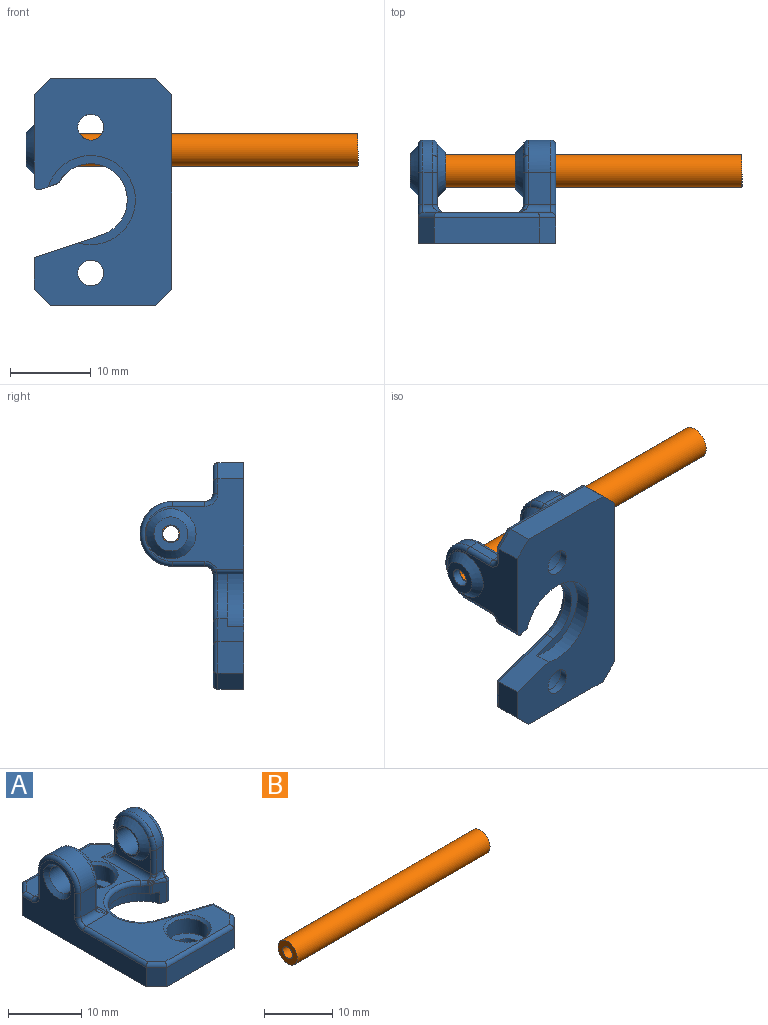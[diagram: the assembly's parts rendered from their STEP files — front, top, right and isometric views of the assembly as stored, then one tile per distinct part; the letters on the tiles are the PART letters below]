
ASSEMBLY  parts=2 mates=1
PART A: 97 faces, bbox 18x28x13.1 mm
  f0: plane 26.8x15.8mm, normal (0,0,1), area 177.3mm2, adj f20,f22,f23,f24,f25,f45,f46,f51
  f1: plane 12.2x11.14mm, normal (1,0,0), area 62.8mm2, adj f3,f34,f49,f56,f58,f60,f62,f64
  f2: plane 24x12.2mm, normal (-1,0,0), area 112.1mm2, adj f3,f26,f36,f48,f63,f65,f67,f69
  f3: plane 28x17mm, normal (0,0,-1), area 336.3mm2, adj f1,f2,f6,f8,f9,f10,f26,f27
  f4: cylinder r=2.85mm len=5.7mm, axis (0,0,-1), area 43mm2, adj f42,f45
  f5: cylinder r=2.85mm len=5.7mm, axis (0,0,-1), area 43mm2, adj f41,f46
  f6: plane 8.43x3.2mm, normal (0.32,0.95,0), area 22.1mm2, adj f3,f7,f8,f30,f31,f53
  f7: cylinder r=4.5mm len=8.77mm, axis (0,0,-1), area 20.9mm2, adj f6,f31,f50,f51,f52,f87
  f8: plane 3.9x3.2mm, normal (1,0,0), area 12.5mm2, adj f3,f6,f27,f55
  f9: plane 3.6x2.01mm, normal (-0.34,-0.94,0), area 5.2mm2, adj f3,f30,f31,f54,f85,f87,f95
  f10: plane 13x3.2mm, normal (0,-1,0), area 41.6mm2, adj f3,f26,f27,f59
  f11: plane 4x1.2mm, normal (0,1,0), area 4.8mm2, adj f20,f28,f62,f76
  f12: plane 6.8x5.78mm, normal (-1,0,0), area 11.6mm2, adj f22,f38,f76,f77,f79,f80
  f13: plane 4.1x1.21mm, normal (0,-1,0), area 4.8mm2, adj f19,f28,f58,f80,f81
  f14: plane 4x2.8mm, normal (0,1,0), area 11.2mm2, adj f23,f29,f71,f93
  f15: plane 4x2.8mm, normal (0,-1,0), area 11.2mm2, adj f25,f29,f67,f89
  f16: plane 6.8x5.78mm, normal (1,0,0), area 11.6mm2, adj f24,f40,f89,f90,f92,f93
  f17: cylinder r=2.05mm len=4.4mm, axis (-1,0,0), area 56.7mm2, adj f36,f39
  f18: cylinder r=2.05mm len=4.1mm, axis (-1,0,0), area 43.8mm2, adj f32,f37
  f19: bspline ~2.84x1.17mm, area 1.4mm2, adj f13,f54,f56,f82,f83
  f20: cylinder r=1mm len=2.8mm, axis (-1,0,0), area 3.1mm2, adj f0,f11,f64,f75
  f21: bspline ~1.22x1.21mm, area 0.1mm2, adj f22,f52,f83,f85
  f22: cylinder r=1mm len=8.5mm, axis (0,-1,0), area 11.5mm2, adj f0,f12,f21,f50,f75,f81,f82
  f23: cylinder r=1mm len=4.4mm, axis (-1,0,0), area 5.7mm2, adj f0,f14,f73,f94
  f24: cylinder r=1mm len=10mm, axis (0,1,0), area 13.2mm2, adj f0,f16,f88,f94
  f25: cylinder r=1mm len=4.4mm, axis (1,0,0), area 5.7mm2, adj f0,f15,f65,f88
  f26: plane 3.2x2mm, normal (-0.71,-0.71,0), area 9.1mm2, adj f2,f3,f10,f61
  f27: plane 3.2x2mm, normal (0.71,-0.71,0), area 9.1mm2, adj f3,f8,f10,f57
  f28: cylinder r=4mm len=8mm, axis (-1,0,0), area 15.1mm2, adj f11,f13,f60,f77,f78,f79
  f29: cylinder r=4mm len=8mm, axis (1,0,0), area 35.2mm2, adj f14,f15,f69,f90,f91,f92
  f30: cylinder r=5.5mm len=11mm, axis (0,0,-1), area 51.7mm2, adj f3,f6,f9,f31
  f31: plane 11x10.75mm, normal (0,0,-1), area 22.2mm2, adj f6,f7,f9,f30,f87
  f32: plane 4.1x4.1mm, normal (-1,0,0), area 9.4mm2, adj f18,f35
  f33: plane 4.2x4.2mm, normal (1,0,0), area 10.1mm2, adj f34,f35
  f34: cone r=2.1mm half-angle=45deg, axis (-1,0,0), area 23.1mm2, adj f1,f33
  f35: cylinder r=1.1mm len=2.2mm, axis (-1,0,0), area 6.9mm2, adj f32,f33
  f36: cone r=2.05mm half-angle=45deg, axis (-1,0,0), area 12.5mm2, adj f2,f17
  f37: plane 4.6x4.6mm, normal (-1,0,0), area 3.4mm2, adj f18,f38
  f38: cone r=2.3mm half-angle=45deg, axis (1,0,0), area 24.9mm2, adj f12,f37,f78
  f39: plane 4.6x4.6mm, normal (1,0,0), area 3.4mm2, adj f17,f40
  f40: cone r=2.3mm half-angle=45deg, axis (-1,0,0), area 24.9mm2, adj f16,f39,f91
  f41: plane 5.73x5.73mm, normal (0,0,1), area 17.6mm2, adj f5,f44
  f42: plane 5.7x5.7mm, normal (0,0,1), area 17.5mm2, adj f4,f43
  f43: cylinder r=1.6mm len=3.2mm, axis (0,0,1), area 10.1mm2, adj f3,f42
  f44: cylinder r=1.6mm len=3.2mm, axis (0,0,1), area 10.1mm2, adj f3,f41
  f45: cone r=2.85mm half-angle=45deg, axis (0,0,1), area 10.8mm2, adj f0,f4
  f46: cone r=2.85mm half-angle=45deg, axis (0,0,1), area 10.8mm2, adj f0,f5
  f47: plane 13x3.2mm, normal (0,1,0), area 41.6mm2, adj f3,f48,f49,f70
  f48: plane 3.2x2mm, normal (-0.71,0.71,0), area 9.1mm2, adj f2,f3,f47,f72
  f49: plane 3.2x2mm, normal (0.71,0.71,0), area 9.1mm2, adj f1,f3,f47,f68
  f50: bspline ~2.4x1.52mm, area 0.8mm2, adj f7,f22,f51,f52
  f51: torus R=5.1mm, axis (0,0,1), area 16mm2, adj f0,f7,f50,f53
  f52: bspline ~0.87x0.62mm, area 0.1mm2, adj f7,f21,f50,f86
  f53: cylinder r=0.6mm len=8.62mm, axis (0.95,-0.32,0), area 8.2mm2, adj f0,f6,f51,f55
  f54: bspline ~2.19x0.8mm, area 1mm2, adj f9,f19,f84,f96
  f55: cylinder r=0.6mm len=3.9mm, axis (0,-1,0), area 3.4mm2, adj f0,f8,f53,f57
  f56: bspline ~1.75x1.38mm, area 1.3mm2, adj f1,f19,f58,f96
  f57: cylinder r=0.6mm len=2.42mm, axis (0.71,0.71,0), area 2.4mm2, adj f0,f27,f55,f59
  f58: cylinder r=0.6mm len=4mm, axis (0,0,-1), area 3.8mm2, adj f1,f13,f56,f60
  f59: cylinder r=0.6mm len=13mm, axis (-1,0,0), area 12mm2, adj f0,f10,f57,f61
  f60: torus R=3.4mm, axis (1,0,0), area 11.2mm2, adj f1,f28,f58,f62
  f61: cylinder r=0.6mm len=2.42mm, axis (-0.71,0.71,0), area 2.4mm2, adj f0,f26,f59,f63
  f62: cylinder r=0.6mm len=4mm, axis (0,0,1), area 3.8mm2, adj f1,f11,f60,f64
  f63: cylinder r=0.6mm len=12.2mm, axis (0,1,0), area 11.4mm2, adj f0,f2,f61,f65
  f64: torus R=1.6mm, axis (1,0,0), area 1.8mm2, adj f1,f20,f62,f66
  f65: torus R=1.6mm, axis (1,0,0), area 1.8mm2, adj f2,f25,f63,f67
  f66: cylinder r=0.6mm len=1.8mm, axis (0,-1,0), area 1.6mm2, adj f0,f1,f64,f68
  f67: cylinder r=0.6mm len=4mm, axis (0,0,-1), area 3.8mm2, adj f2,f15,f65,f69
  f68: cylinder r=0.6mm len=2.42mm, axis (0.71,-0.71,0), area 2.4mm2, adj f0,f49,f66,f70
  f69: torus R=3.4mm, axis (1,0,0), area 11.2mm2, adj f2,f29,f67,f71
  f70: cylinder r=0.6mm len=13mm, axis (-1,0,0), area 12mm2, adj f0,f47,f68,f72
  f71: cylinder r=0.6mm len=4mm, axis (0,0,1), area 3.8mm2, adj f2,f14,f69,f73
  f72: cylinder r=0.6mm len=2.42mm, axis (-0.71,-0.71,0), area 2.4mm2, adj f0,f48,f70,f74
  f73: torus R=1.6mm, axis (1,0,0), area 1.8mm2, adj f2,f23,f71,f74
  f74: cylinder r=0.6mm len=1.8mm, axis (0,1,0), area 1.6mm2, adj f0,f2,f72,f73
  f75: bspline ~1.6x1.6mm, area 0.6mm2, adj f20,f22,f76
  f76: cylinder r=0.6mm len=4mm, axis (0,0,-1), area 3.8mm2, adj f11,f12,f75,f77
  f77: torus R=3.4mm, axis (1,0,0), area 2mm2, adj f12,f28,f76,f78
  f78: bspline ~7.3x2.87mm, area 6.8mm2, adj f28,f38,f77,f79
  f79: torus R=3.4mm, axis (1,0,0), area 2mm2, adj f12,f28,f78,f80
  f80: cylinder r=0.6mm len=4mm, axis (0,0,1), area 3.8mm2, adj f12,f13,f79,f81
  f81: torus R=1.6mm, axis (0,-1,0), area 0.1mm2, adj f13,f22,f80,f82
  f82: bspline ~0.82x0.73mm, area 0.3mm2, adj f19,f22,f81,f83
  f83: bspline ~0.9x0.78mm, area 0.3mm2, adj f19,f21,f82,f84
  f84: sphere r=0.6mm, area 0.1mm2, adj f54,f83,f85
  f85: bspline ~0.93x0.89mm, area 0.2mm2, adj f9,f21,f84,f86
  f86: sphere r=0.6mm, area 0.2mm2, adj f52,f85,f87
  f87: cylinder r=0.6mm len=1.41mm, axis (0,0,-1), area 0.6mm2, adj f7,f9,f31,f86
  f88: bspline ~1.6x1.6mm, area 0.6mm2, adj f24,f25,f89
  f89: cylinder r=0.6mm len=4mm, axis (0,0,1), area 3.8mm2, adj f15,f16,f88,f90
  f90: torus R=3.4mm, axis (1,0,0), area 2mm2, adj f16,f29,f89,f91
  f91: bspline ~7.3x2.87mm, area 6.8mm2, adj f29,f40,f90,f92
  f92: torus R=3.4mm, axis (1,0,0), area 2mm2, adj f16,f29,f91,f93
  f93: cylinder r=0.6mm len=4mm, axis (0,0,-1), area 3.8mm2, adj f14,f16,f92,f94
  f94: bspline ~1.6x1.6mm, area 0.6mm2, adj f23,f24,f93
  f95: cylinder r=0.6mm len=3.34mm, axis (0,0,-1), area 3.8mm2, adj f1,f3,f9,f96
  f96: sphere r=0.6mm, area 0.5mm2, adj f54,f56,f95
PART B: 4 faces, bbox 40x4x4 mm
  f0: cylinder r=1mm len=40mm, axis (-1,0,0), area 251.3mm2, adj f2,f3
  f1: cylinder r=2mm len=40mm, axis (-1,0,0), area 502.7mm2, adj f2,f3
  f2: plane 4x4mm, normal (1,0,0), area 9.4mm2, adj f0,f1
  f3: plane 4x4mm, normal (-1,0,0), area 9.4mm2, adj f0,f1
PLACE A rot(axis=(0,-0.71,-0.71),180deg) t=(273.07,203.73,-143.18)mm
PLACE B rot(axis=(0,-0.71,-0.71),180deg) t=(306.07,212.73,-136.98)mm
MATE fastened B.f0 <-> A.f17  axis (-1,0,0) through (266.07,212.73,-136.98)mm
